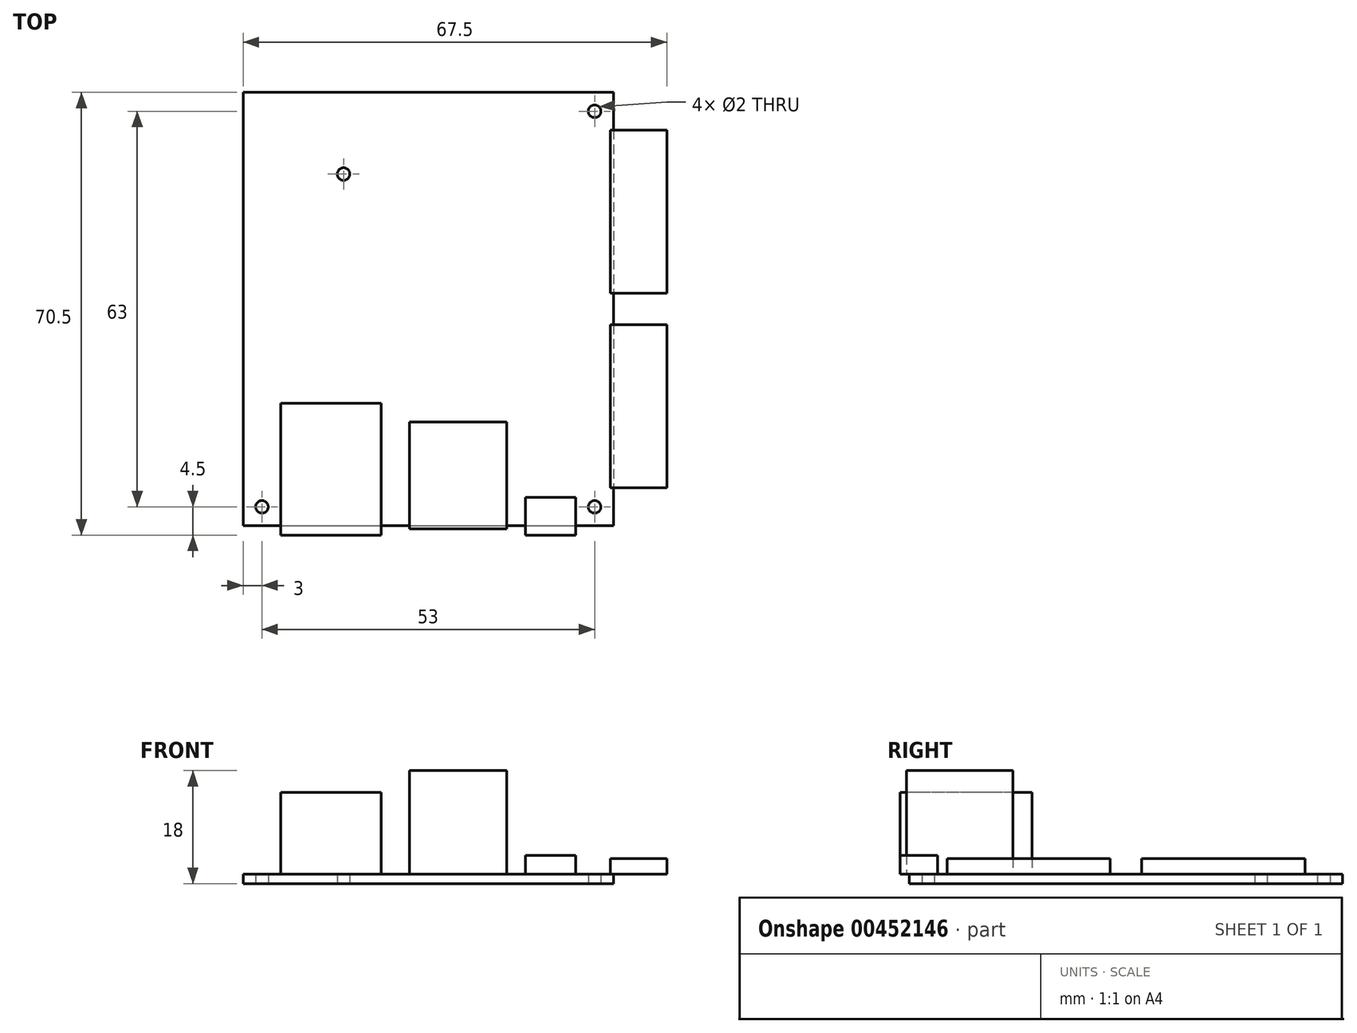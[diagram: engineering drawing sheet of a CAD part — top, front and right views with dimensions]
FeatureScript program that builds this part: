
annotation { "Feature Type Name" : "Feature", "Feature Type Description" : "" }
export const myFeature = defineFeature(function(context is Context, id is Id, definition is map)
    precondition{}
    {
        {
            var Q0;
            Q0=qCreatedBy(makeId("Top.planeOp"),FACE);
            var sketch = newSketch(context, id + "F0", { "sketchPlane" : qUnion([Q0])});
            skLineSegment(sketch, "E0.bottom", {"start": v(-29.5, 34.5) * mm, "end": v(29.5, 34.5) * mm});
            skLineSegment(sketch, "E0.top", {"start": v(-29.5, -34.5) * mm, "end": v(29.5, -34.5) * mm});
            skLineSegment(sketch, "E0.left", {"start": v(-29.5, 34.5) * mm, "end": v(-29.5, -34.5) * mm});
            skLineSegment(sketch, "E0.right", {"start": v(29.5, 34.5) * mm, "end": v(29.5, -34.5) * mm});
            skPoint(sketch, "E0.middle", {"position": v(0, 0) * mm});
            skCircle(sketch, "E1", {"center": v(26.5, 31.5) * mm, "radius": 1 * mm});
            skCircle(sketch, "E2.MirrorC", {"center": v(26.5, -31.5) * mm, "radius": 1 * mm});
            skCircle(sketch, "E3.MirrorC", {"center": v(-26.5, -31.5) * mm, "radius": 1 * mm});
            skCircle(sketch, "E4", {"center": v(-13.5, 21.5) * mm, "radius": 1 * mm});
            skSolve(sketch);
        }
        {
            var Q0;
            Q0=makeQuery(id+"F0.imprint","IMPRINT",FACE,{"disambiguationData":[TD([[makeQuery(id+"F0.imprint","IMPRINT",EDGE,{"derivedFrom":sQuery(id+"F0.wireOp",EDGE,"E0.bottom")}),-1.0]])]});
            extrude(context, id + "F1", {"entities" : qUnion([Q0]), "depth" : 1.5 * mm});
        }
        {
            var Q0;
            Q0=makeQuery(id+"F1.opExtrude","CAP_FACE",FACE,{"disambiguationData":[OSD([sQuery(id+"F0.wireOp",EDGE,"E0.bottom"),sQuery(id+"F0.wireOp",EDGE,"E0.top"),sQuery(id+"F0.wireOp",EDGE,"E0.left"),sQuery(id+"F0.wireOp",EDGE,"E0.right"),sQuery(id+"F0.wireOp",EDGE,"E1"),sQuery(id+"F0.wireOp",EDGE,"E2.MirrorC"),sQuery(id+"F0.wireOp",EDGE,"E3.MirrorC"),sQuery(id+"F0.wireOp",EDGE,"E4")])],"isStart":false});
            var sketch = newSketch(context, id + "F2", { "sketchPlane" : qUnion([Q0])});
            skLineSegment(sketch, "E5.bottom", {"start": v(15.5, -30) * mm, "end": v(23.5, -30) * mm});
            skLineSegment(sketch, "E5.top", {"start": v(15.5, -36) * mm, "end": v(23.5, -36) * mm});
            skLineSegment(sketch, "E5.left", {"start": v(15.5, -30) * mm, "end": v(15.5, -36) * mm});
            skLineSegment(sketch, "E5.right", {"start": v(23.5, -30) * mm, "end": v(23.5, -36) * mm});
            skLineSegment(sketch, "E6.bottom", {"start": v(-23.5, -15) * mm, "end": v(-7.5, -15) * mm});
            skLineSegment(sketch, "E6.top", {"start": v(-23.5, -36) * mm, "end": v(-7.5, -36) * mm});
            skLineSegment(sketch, "E6.left", {"start": v(-23.5, -15) * mm, "end": v(-23.5, -36) * mm});
            skLineSegment(sketch, "E6.right", {"start": v(-7.5, -15) * mm, "end": v(-7.5, -36) * mm});
            skLineSegment(sketch, "E7.bottom", {"start": v(-3, -18) * mm, "end": v(12.5, -18) * mm});
            skLineSegment(sketch, "E7.top", {"start": v(-3, -35) * mm, "end": v(12.5, -35) * mm});
            skLineSegment(sketch, "E7.left", {"start": v(-3, -18) * mm, "end": v(-3, -35) * mm});
            skLineSegment(sketch, "E7.right", {"start": v(12.5, -18) * mm, "end": v(12.5, -35) * mm});
            skLineSegment(sketch, "E8.bottom", {"start": v(29, 28.5) * mm, "end": v(38, 28.5) * mm});
            skLineSegment(sketch, "E8.top", {"start": v(29, 2.5) * mm, "end": v(38, 2.5) * mm});
            skLineSegment(sketch, "E8.left", {"start": v(29, 28.5) * mm, "end": v(29, 2.5) * mm});
            skLineSegment(sketch, "E8.right", {"start": v(38, 28.5) * mm, "end": v(38, 2.5) * mm});
            skLineSegment(sketch, "E9.MirrorCS", {"start": v(29, -2.5) * mm, "end": v(38, -2.5) * mm});
            skLineSegment(sketch, "E10.MirrorCS", {"start": v(29, -28.5) * mm, "end": v(29, -2.5) * mm});
            skLineSegment(sketch, "E11.MirrorCS", {"start": v(29, -28.5) * mm, "end": v(38, -28.5) * mm});
            skLineSegment(sketch, "E12.MirrorCS", {"start": v(38, -28.5) * mm, "end": v(38, -2.5) * mm});
            skSolve(sketch);
        }
        {
            var Q0;
            {var subQ0=sQuery(id+"F2.wireOp",EDGE,"E5.top");Q0=makeQuery(id+"F2.imprint","IMPRINT",FACE,{"disambiguationData":[TD([[makeQuery(id+"F2.imprint","IMPRINT",EDGE,{"derivedFrom":subQ0}),1.0]])]});}
            var Q1;
            {var subQ0=sQuery(id+"F2.wireOp",EDGE,"E5.bottom");Q1=makeQuery(id+"F2.imprint","IMPRINT",FACE,{"disambiguationData":[TD([[makeQuery(id+"F2.imprint","IMPRINT",EDGE,{"derivedFrom":subQ0}),-1.0]])]});}
            extrude(context, id + "F3", {"entities" : qUnion([Q0, Q1]), "operationType" : NewBodyOperationType.ADD, "depth" : 3 * mm});
        }
        {
            var Q0;
            {var subQ0=sQuery(id+"F2.wireOp",EDGE,"E7.bottom");Q0=makeQuery(id+"F2.imprint","IMPRINT",FACE,{"disambiguationData":[TD([[makeQuery(id+"F2.imprint","IMPRINT",EDGE,{"derivedFrom":subQ0}),-1.0]])]});}
            var Q1;
            {var subQ0=sQuery(id+"F2.wireOp",EDGE,"E7.top");Q1=makeQuery(id+"F2.imprint","IMPRINT",FACE,{"disambiguationData":[TD([[makeQuery(id+"F2.imprint","IMPRINT",EDGE,{"derivedFrom":subQ0}),1.0]])]});}
            extrude(context, id + "F4", {"entities" : qUnion([Q0, Q1]), "operationType" : NewBodyOperationType.ADD, "depth" : 16.5 * mm});
        }
        {
            var Q0;
            {var subQ0=sQuery(id+"F2.wireOp",EDGE,"E6.bottom");Q0=makeQuery(id+"F2.imprint","IMPRINT",FACE,{"disambiguationData":[TD([[makeQuery(id+"F2.imprint","IMPRINT",EDGE,{"derivedFrom":subQ0}),-1.0]])]});}
            var Q1;
            {var subQ0=sQuery(id+"F2.wireOp",EDGE,"E6.top");Q1=makeQuery(id+"F2.imprint","IMPRINT",FACE,{"disambiguationData":[TD([[makeQuery(id+"F2.imprint","IMPRINT",EDGE,{"derivedFrom":subQ0}),1.0]])]});}
            extrude(context, id + "F5", {"entities" : qUnion([Q0, Q1]), "operationType" : NewBodyOperationType.ADD, "depth" : 13 * mm});
        }
        {
            var Q0;
            {var subQ0=sQuery(id+"F2.wireOp",EDGE,"E8.left");Q0=makeQuery(id+"F2.imprint","IMPRINT",FACE,{"disambiguationData":[TD([[makeQuery(id+"F2.imprint","IMPRINT",EDGE,{"derivedFrom":subQ0}),1.0]])]});}
            var Q1;
            {var subQ0=sQuery(id+"F2.wireOp",EDGE,"E8.right");Q1=makeQuery(id+"F2.imprint","IMPRINT",FACE,{"disambiguationData":[TD([[makeQuery(id+"F2.imprint","IMPRINT",EDGE,{"derivedFrom":subQ0}),-1.0]])]});}
            var Q2;
            {var subQ0=sQuery(id+"F2.wireOp",EDGE,"E10.MirrorCS");Q2=makeQuery(id+"F2.imprint","IMPRINT",FACE,{"disambiguationData":[TD([[makeQuery(id+"F2.imprint","IMPRINT",EDGE,{"derivedFrom":subQ0}),-1.0]])]});}
            var Q3;
            {var subQ0=sQuery(id+"F2.wireOp",EDGE,"E12.MirrorCS");Q3=makeQuery(id+"F2.imprint","IMPRINT",FACE,{"disambiguationData":[TD([[makeQuery(id+"F2.imprint","IMPRINT",EDGE,{"derivedFrom":subQ0}),1.0]])]});}
            extrude(context, id + "F6", {"entities" : qUnion([Q0, Q1, Q2, Q3]), "operationType" : NewBodyOperationType.ADD, "depth" : 2.5 * mm});
        }
    });
